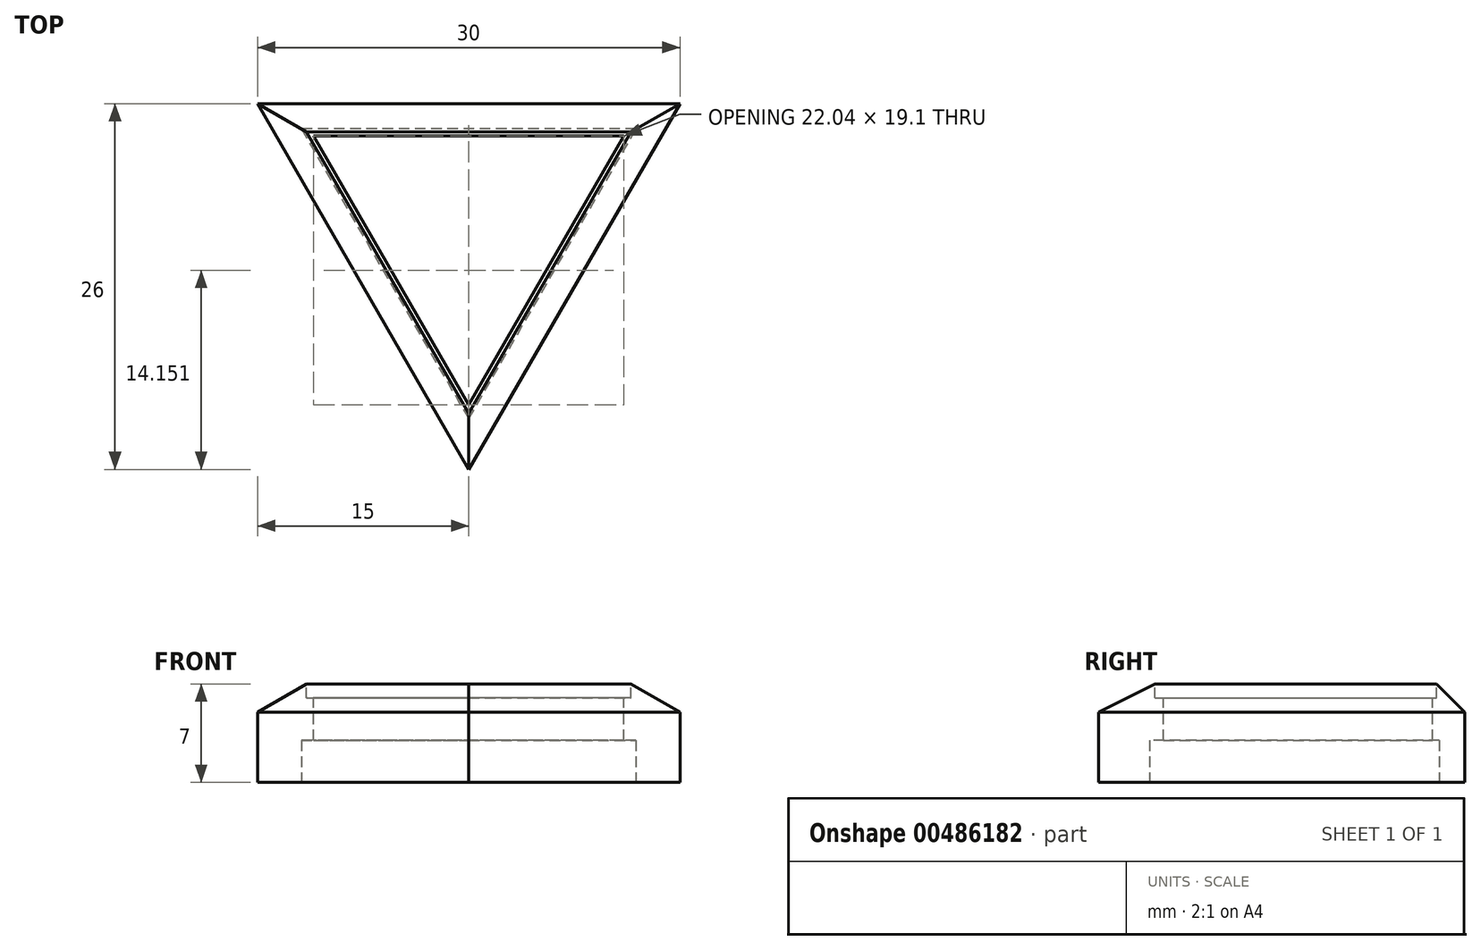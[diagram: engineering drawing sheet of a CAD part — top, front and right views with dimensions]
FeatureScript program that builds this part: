
annotation { "Feature Type Name" : "Feature", "Feature Type Description" : "" }
export const myFeature = defineFeature(function(context is Context, id is Id, definition is map)
    precondition{}
    {
        {
            var Q0;
            Q0=qCreatedBy(makeId("Top.planeOp"),FACE);
            var sketch = newSketch(context, id + "F0", { "sketchPlane" : qUnion([Q0])});
            skLineSegment(sketch, "E0", {"start": v(-15, 0) * mm, "end": v(0, -26) * mm});
            skLineSegment(sketch, "E1", {"start": v(0, -26) * mm, "end": v(15, 0) * mm});
            skLineSegment(sketch, "E2", {"start": v(15, 0) * mm, "end": v(-15, 0) * mm});
            skSolve(sketch);
        }
        {
            var Q0;
            Q0=makeQuery(id+"F0.imprint","IMPRINT",FACE,{"disambiguationData":[TD([[makeQuery(id+"F0.imprint","IMPRINT",EDGE,{"derivedFrom":sQuery(id+"F0.wireOp",EDGE,"E0")}),1.0]])]});
            extrude(context, id + "F1", {"entities" : qUnion([Q0]), "depth" : 5 * mm});
        }
        {
            var Q0;
            Q0=makeQuery(id+"F1.opExtrude","CAP_FACE",FACE,{"disambiguationData":[OSD([sQuery(id+"F0.wireOp",EDGE,"E0"),sQuery(id+"F0.wireOp",EDGE,"E1"),sQuery(id+"F0.wireOp",EDGE,"E2")])],"isStart":false});
            cPlane(context, id + "F2", {"entities" : qUnion([Q0]), "cplaneType" : CPlaneType.OFFSET, "offset" : 2 * mm, "width" : 150 * mm, "height" : 150 * mm});
        }
        {
            var Q0;
            Q0=qCreatedBy(id+"F2.planeOp",FACE);
            var sketch = newSketch(context, id + "F3", { "sketchPlane" : qUnion([Q0])});
            skLineSegment(sketch, "E3.0", {"start": v(11.54, -2) * mm, "end": v(-11.54, -2) * mm});
            skLineSegment(sketch, "E3.1", {"start": v(0, -22) * mm, "end": v(11.54, -2) * mm});
            skLineSegment(sketch, "E3.2", {"start": v(-11.54, -2) * mm, "end": v(0, -22) * mm});
            skSolve(sketch);
        }
        {
            var Q1;
            Q1=makeQuery(id+"F1.opExtrude","CAP_FACE",FACE,{"disambiguationData":[OSD([sQuery(id+"F0.wireOp",EDGE,"E0"),sQuery(id+"F0.wireOp",EDGE,"E1"),sQuery(id+"F0.wireOp",EDGE,"E2")])],"isStart":false});
            var Q2;
            Q2=makeQuery(id+"F3.imprint","IMPRINT",FACE,{"disambiguationData":[TD([[makeQuery(id+"F3.imprint","IMPRINT",EDGE,{"derivedFrom":sQuery(id+"F3.wireOp",EDGE,"E3.0")}),1.0]])]});
            loft(context, id + "F4", {"operationType" : NewBodyOperationType.ADD, "sheetProfilesArray" : [{ "sheetProfileEntities" : qUnion([Q1]) }, { "sheetProfileEntities" : qUnion([Q2]) }]});
        }
        {
            var Q0;
            Q0=makeQuery(id+"F1.opExtrude","CAP_FACE",FACE,{"disambiguationData":[OSD([sQuery(id+"F0.wireOp",EDGE,"E0"),sQuery(id+"F0.wireOp",EDGE,"E1"),sQuery(id+"F0.wireOp",EDGE,"E2")])],"isStart":true});
            var sketch = newSketch(context, id + "F5", { "sketchPlane" : qUnion([Q0])});
            skLineSegment(sketch, "E4.0", {"start": v(-11.88, 1.8) * mm, "end": v(0, 22.4) * mm});
            skLineSegment(sketch, "E4.1", {"start": v(11.88, 1.8) * mm, "end": v(-11.88, 1.8) * mm});
            skLineSegment(sketch, "E4.2", {"start": v(0, 22.4) * mm, "end": v(11.88, 1.8) * mm});
            skSolve(sketch);
        }
        {
            var Q0;
            Q0=makeQuery(id+"F4.opLoft","CAP_FACE",FACE,{"disambiguationData":[OSD([makeQuery(id+"F3.imprint","IMPRINT",FACE,{"disambiguationData":[TD([[makeQuery(id+"F3.imprint","IMPRINT",EDGE,{"derivedFrom":sQuery(id+"F3.wireOp",EDGE,"E3.0")}),1.0]])]})])],"isStart":true});
            extrude(context, id + "F6", {"entities" : qUnion([Q0]), "operationType" : NewBodyOperationType.REMOVE, "oppositeDirection" : true, "depth" : 1 * mm});
        }
        {
            var Q0;
            Q0=makeQuery(id+"F6.boolean.opBoolean","COPY",FACE,{"derivedFrom":makeQuery(id+"F6.opExtrude","CAP_FACE",FACE,{"disambiguationData":[OSD([makeQuery(id+"F3.imprint","IMPRINT",FACE,{"disambiguationData":[TD([[makeQuery(id+"F3.imprint","IMPRINT",EDGE,{"derivedFrom":sQuery(id+"F3.wireOp",EDGE,"E3.0")}),1.0]])]})])],"isStart":false})});
            var sketch = newSketch(context, id + "F7", { "sketchPlane" : qUnion([Q0])});
            skLineSegment(sketch, "E5.0", {"start": v(11.02, -2.3) * mm, "end": v(-11.02, -2.3) * mm});
            skLineSegment(sketch, "E5.1", {"start": v(0, -21.4) * mm, "end": v(11.02, -2.3) * mm});
            skLineSegment(sketch, "E5.2", {"start": v(-11.02, -2.3) * mm, "end": v(0, -21.4) * mm});
            skSolve(sketch);
        }
        {
            var Q0;
            Q0=makeQuery(id+"F7.imprint","IMPRINT",FACE,{"disambiguationData":[TD([[makeQuery(id+"F7.imprint","IMPRINT",EDGE,{"derivedFrom":sQuery(id+"F7.wireOp",EDGE,"E5.0")}),1.0]])]});
            extrude(context, id + "F8", {"entities" : qUnion([Q0]), "operationType" : NewBodyOperationType.REMOVE, "oppositeDirection" : true, "depth" : 3 * mm});
        }
        {
            var Q0;
            Q0=makeQuery(id+"F5.imprint","IMPRINT",FACE,{"disambiguationData":[TD([[makeQuery(id+"F5.imprint","IMPRINT",EDGE,{"derivedFrom":sQuery(id+"F5.wireOp",EDGE,"E4.0")}),-1.0]])]});
            var Q1;
            Q1=makeQuery(id+"F8.boolean.opBoolean","COPY",FACE,{"derivedFrom":makeQuery(id+"F8.opExtrude","CAP_FACE",FACE,{"disambiguationData":[OSD([sQuery(id+"F7.wireOp",EDGE,"E5.0"),sQuery(id+"F7.wireOp",EDGE,"E5.1"),sQuery(id+"F7.wireOp",EDGE,"E5.2")])],"isStart":false})});
            extrude(context, id + "F9", {"entities" : qUnion([Q0]), "operationType" : NewBodyOperationType.REMOVE, "endBound" : BoundingType.UP_TO_SURFACE, "oppositeDirection" : true, "endBoundEntityFace" : qUnion([Q1]), "depth" : 2.8 * mm});
        }
    });
